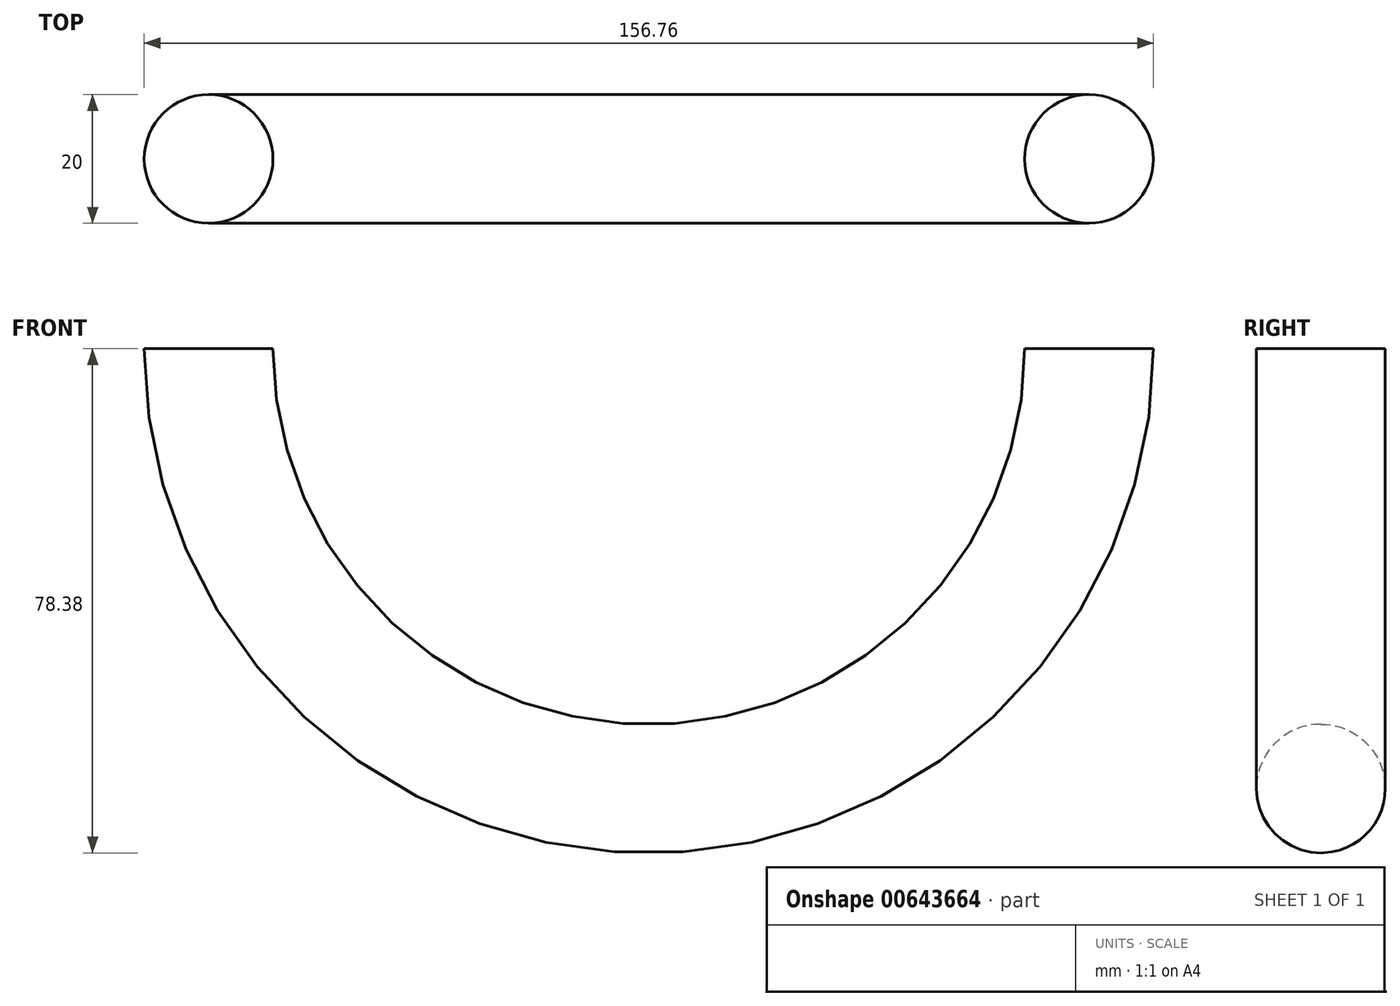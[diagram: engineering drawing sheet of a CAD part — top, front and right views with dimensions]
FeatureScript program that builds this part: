
annotation { "Feature Type Name" : "Feature", "Feature Type Description" : "" }
export const myFeature = defineFeature(function(context is Context, id is Id, definition is map)
    precondition{}
    {
        {
            var Q0;
            Q0=qCreatedBy(makeId("Top.planeOp"),FACE);
            var sketch = newSketch(context, id + "F0", { "sketchPlane" : qUnion([Q0])});
            skCircle(sketch, "E0", {"center": v(-68.38, 0) * mm, "radius": 10 * mm});
            skLineSegment(sketch, "E1", {"start": v(0, 67.3) * mm, "end": v(0, -42.97) * mm});
            skSolve(sketch);
        }
        {
            var Q0;
            Q0=makeQuery(id+"F0.imprint","IMPRINT",FACE,{"disambiguationData":[TD([[makeQuery(id+"F0.imprint","IMPRINT",EDGE,{"derivedFrom":sQuery(id+"F0.wireOp",EDGE,"E0")}),1.0]])]});
            var Q1;
            Q1=sQuery(id+"F0.wireOp",EDGE,"E1");
            revolve(context, id + "F1", {"entities" : qUnion([Q0]), "axis" : qUnion([Q1]), "revolveType" : RevolveType.ONE_DIRECTION, "angle" : 180 * degree});
        }
    });
